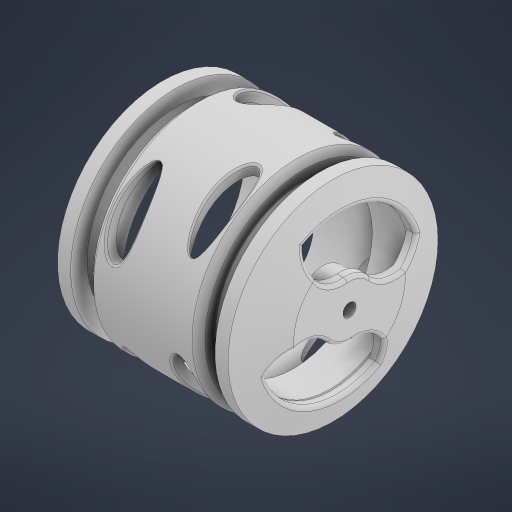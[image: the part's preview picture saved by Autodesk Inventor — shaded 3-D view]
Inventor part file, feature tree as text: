
AUTODESK INVENTOR PART (.ipt)
format: ipt  version: 2024 (Build 280153000, 153)  size: 1,240,064 bytes
history: native  units: mm
features: sketch x6, other x4, extrude x4, revolve x2, pattern_circular x2, chamfer x2, shell x1, fillet x1
ambient origin geometry x8: Origin, YZ Plane, XZ Plane, XY Plane, X Axis, Y Axis, Z Axis, Center Point
bodies: Body1 (feature_tree)
feature tree (22):
  other  "Твердое тело1"
  revolve  "Вращение1"
  revolve  "Вращение2"
  shell  "Оболочка1"  Thickness=32.0mm
  extrude  "Выдавливание1"  Depth=27.0mm
  extrude  "Выдавливание2"  Depth=5.0mm
  other  "wheel"
  extrude  "Выдавливание3"  Depth=34.0mm
  pattern_circular  "Круговой массив1"  [2 undecoded]
  other  "РабПлоскость1"
  extrude  "Выдавливание4"  TaperAngle=90.0deg  [1 undecoded]
  pattern_circular  "Круговой массив2"  [2 undecoded]
  chamfer  "Фаска1"  Distance=5.0mm
  chamfer  "Фаска2"  Angle=90.0deg  [1 undecoded]
  fillet  "Сопряжение1"  Radius=3.0mm
  sketch  "Эскиз1"
  sketch  "Эскиз2"
  sketch  "Эскиз3"
  sketch  "Эскиз4"
  sketch  "Эскиз6"
  sketch  "Эскиз7"
  other  "ЭлементСетки1"
note: 6 required parameter values undecoded (feature->parameter linkage not recoverable at this tier; creation-order binding heuristic only, values carry confidence <= 0.55)
